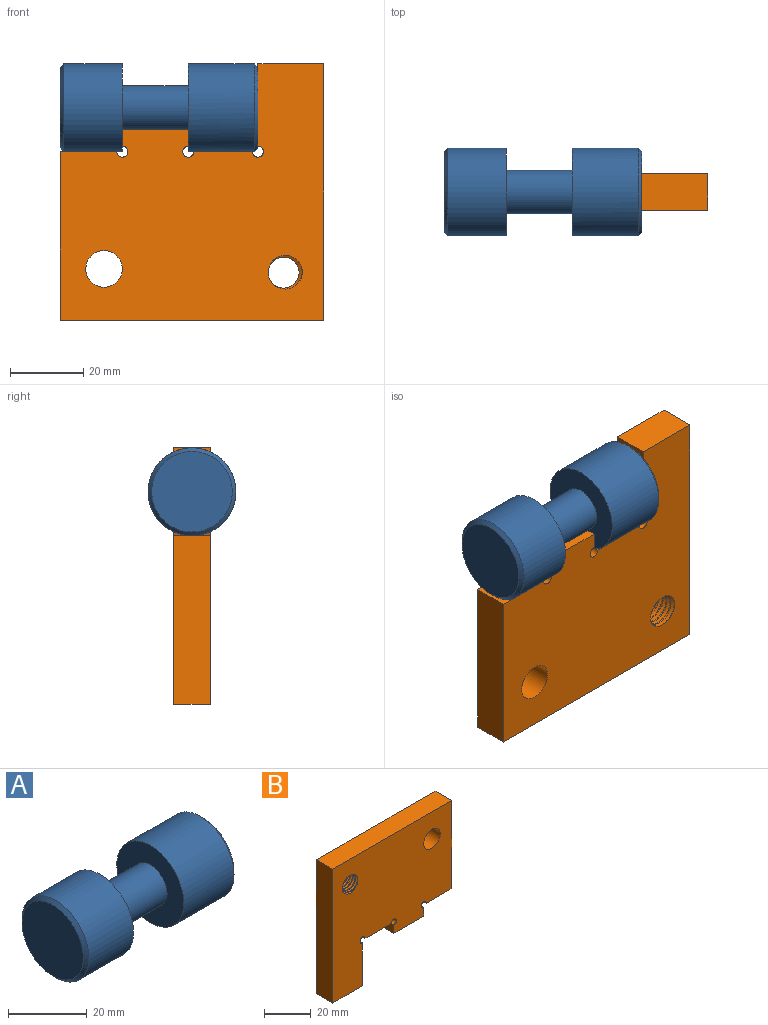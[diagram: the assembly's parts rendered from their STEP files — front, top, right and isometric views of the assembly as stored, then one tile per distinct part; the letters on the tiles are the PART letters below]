
ASSEMBLY  parts=2 mates=1
PART A: 9 faces, bbox 54x24x24 mm
  f0: plane 22x22mm, normal (-1,0,0), area 380.1mm2, adj f8
  f1: plane 22x22mm, normal (1,0,0), area 380.1mm2, adj f7
  f2: cylinder r=12mm len=24mm, axis (-1,0,0), area 1357.2mm2, adj f3,f7
  f3: plane 24x24mm, normal (-1,0,0), area 339.3mm2, adj f2,f4
  f4: cylinder r=6mm len=18mm, axis (-1,0,0), area 678.6mm2, adj f3,f5
  f5: plane 24x24mm, normal (1,0,0), area 339.3mm2, adj f4,f6
  f6: cylinder r=12mm len=24mm, axis (-1,0,0), area 1206.4mm2, adj f5,f8
  f7: cone r=12mm half-angle=45deg, axis (-1,0,0), area 102.2mm2, adj f1,f2
  f8: cone r=11mm half-angle=45deg, axis (1,0,0), area 102.2mm2, adj f0,f6
PART B: 20 faces, bbox 72.4x11.8x70.4 mm
  f0: cylinder r=1.5mm len=10mm, axis (0,1,0), area 70.7mm2, adj f1,f12,f14,f15
  f1: plane 16x10mm, normal (0,0,-1), area 160mm2, adj f0,f2,f14,f15
  f2: cylinder r=1.5mm len=10mm, axis (0,1,0), area 70.7mm2, adj f1,f3,f14,f15
  f3: plane 10x4.5mm, normal (-1,0,0), area 45mm2, adj f2,f4,f14,f15
  f4: plane 18x10mm, normal (0,0,-1), area 180mm2, adj f3,f5,f14,f15
  f5: plane 10x4.5mm, normal (1,0,0), area 45mm2, adj f4,f6,f14,f15
  f6: cylinder r=1.5mm len=10mm, axis (0,1,0), area 70.7mm2, adj f5,f7,f14,f15
  f7: plane 15.5x10mm, normal (0,0,-1), area 155mm2, adj f6,f8,f14,f15
  f8: plane 46x10mm, normal (1,0,0), area 460mm2, adj f7,f9,f14,f15
  f9: plane 72x10mm, normal (0,0,1), area 720mm2, adj f8,f10,f14,f15
  f10: plane 70x10mm, normal (-1,0,0), area 700mm2, adj f9,f11,f14,f15
  f11: plane 18x10mm, normal (0,0,-1), area 180mm2, adj f10,f12,f14,f15
  f12: plane 22.5x10mm, normal (1,0,0), area 225mm2, adj f0,f11,f14,f15
  f13: cylinder r=5mm len=10mm, axis (0,1,0), area 314.2mm2, adj f14,f15
  f14: plane 72.44x70.44mm, normal (0,-1,0), area 3690.5mm2, adj f0,f1,f2,f3,f4,f5,f6,f7
  f15: plane 72.44x70.44mm, normal (0,1,0), area 3690.5mm2, adj f0,f1,f2,f3,f4,f5,f6,f7
  f16: bspline ~11.69x11.22mm, area 180.3mm2, adj f14,f15,f18,f19
  f17: bspline ~11.69x11.22mm, area 184.5mm2, adj f14,f15,f18,f19
  f18: bspline ~11.85x10.69mm, area 46.1mm2, adj f14,f15,f16,f17
  f19: cylinder r=4.25mm len=10mm, axis (0,-1,0), area 128.7mm2, adj f14,f15,f16,f17
PLACE A t=(43.93,15.29,-15.1)mm
PLACE B rot(axis=(0,-1,0),180deg) t=(115.93,20.29,-3.1)mm fixed
MATE fastened B.f12 <-> A.f2  axis (-1,0,0) through (97.93,15.29,-15.1)mm
